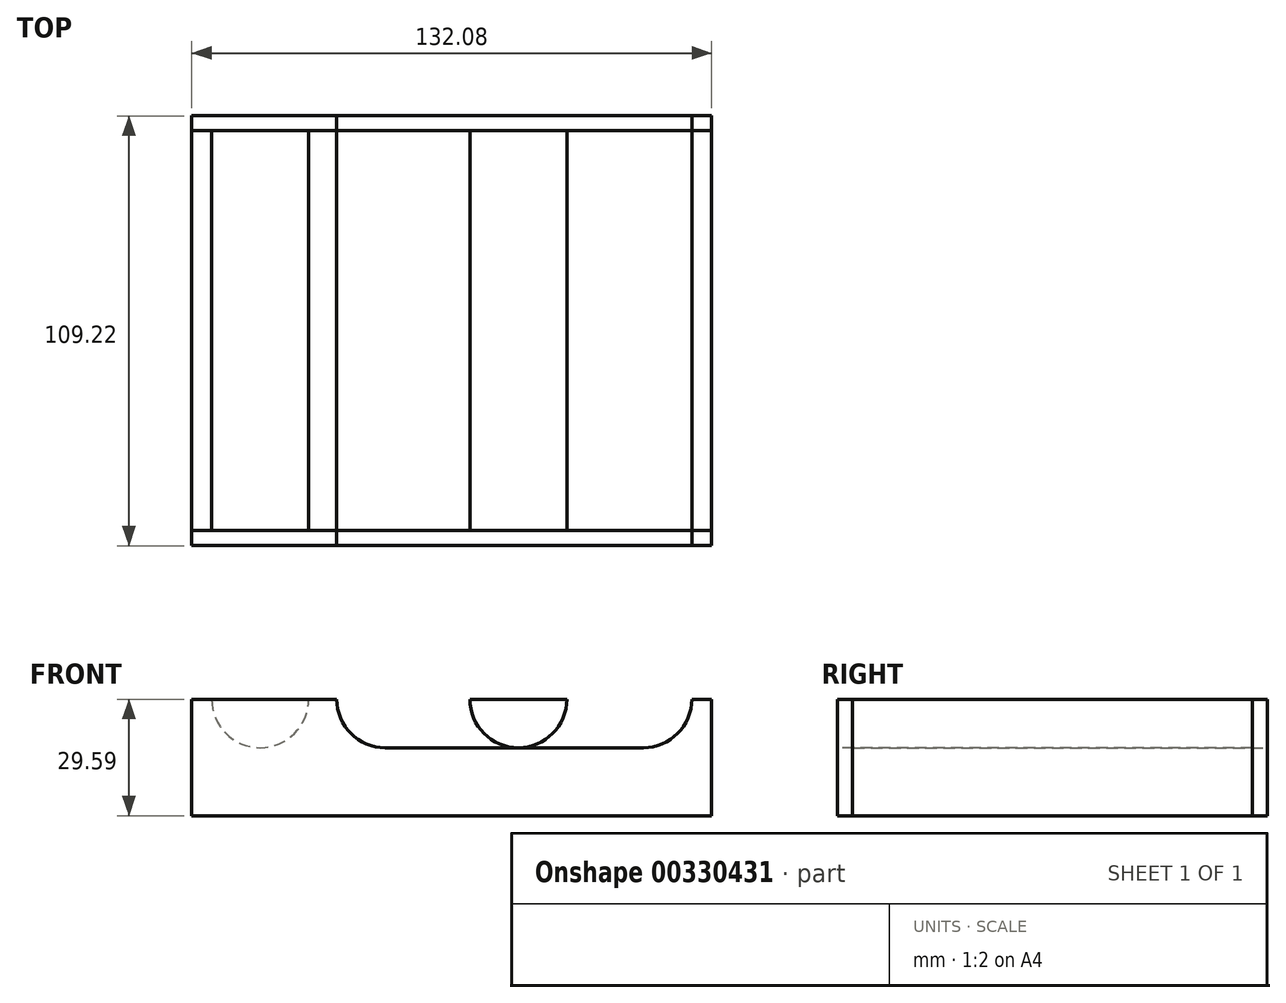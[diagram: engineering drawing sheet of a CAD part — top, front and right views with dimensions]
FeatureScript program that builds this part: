
annotation { "Feature Type Name" : "Feature", "Feature Type Description" : "" }
export const myFeature = defineFeature(function(context is Context, id is Id, definition is map)
    precondition{}
    {
        {
            var Q0;
            Q0=qCreatedBy(makeId("Top.planeOp"),FACE);
            var sketch = newSketch(context, id + "F0", { "sketchPlane" : qUnion([Q0])});
            skLineSegment(sketch, "E0.bottom", {"start": v(-43.55, 68.97) * mm, "end": v(88.53, 68.97) * mm});
            skLineSegment(sketch, "E0.top", {"start": v(-43.55, -32.63) * mm, "end": v(88.53, -32.63) * mm});
            skLineSegment(sketch, "E0.left", {"start": v(-43.55, 68.97) * mm, "end": v(-43.55, -32.63) * mm});
            skLineSegment(sketch, "E0.right", {"start": v(88.53, 68.97) * mm, "end": v(88.53, -32.63) * mm});
            skSolve(sketch);
        }
        {
            var Q0;
            Q0=makeQuery(id+"F0.imprint","IMPRINT",FACE,{"disambiguationData":[TD([[makeQuery(id+"F0.imprint","IMPRINT",EDGE,{"derivedFrom":sQuery(id+"F0.wireOp",EDGE,"E0.bottom")}),-1.0]])]});
            extrude(context, id + "F1", {"entities" : qUnion([Q0]), "depth" : 17.27 * mm});
        }
        {
            var Q0;
            Q0=makeQuery(id+"F1.opExtrude","SWEPT_FACE",FACE,{"disambiguationData":[OSD([sQuery(id+"F0.wireOp",EDGE,"E0.top")])]});
            var sketch = newSketch(context, id + "F2", { "sketchPlane" : qUnion([Q0])});
            skLineSegment(sketch, "E1", {"start": v(-26.19, 47.06) * mm, "end": v(-26.19, 17.27) * mm, "construction": true});
            skCircle(sketch, "E2", {"center": v(-26.19, 29.6) * mm, "radius": 12.32 * mm});
            skLineSegment(sketch, "E3", {"start": v(22.49, 17.27) * mm, "end": v(22.49, 64.89) * mm, "construction": true});
            skPoint(sketch, "E3.endSnap0", {"position": v(22.49, 17.27) * mm});
            skCircle(sketch, "E4.1.0.0", {"center": v(5.56, 29.6) * mm, "radius": 12.32 * mm});
            skLineSegment(sketch, "E4.direction1", {"start": v(-26.19, 29.6) * mm, "end": v(5.56, 29.6) * mm, "construction": true});
            skCircle(sketch, "E5.MirrorC", {"center": v(39.41, 29.6) * mm, "radius": 12.32 * mm});
            skCircle(sketch, "E6.MirrorC", {"center": v(71.16, 29.6) * mm, "radius": 12.32 * mm});
            skLineSegment(sketch, "E7", {"start": v(-43.55, 17.27) * mm, "end": v(-43.55, 29.6) * mm});
            skLineSegment(sketch, "E8", {"start": v(-43.55, 29.6) * mm, "end": v(88.53, 29.6) * mm});
            skLineSegment(sketch, "E9", {"start": v(88.53, 29.6) * mm, "end": v(88.53, 17.27) * mm});
            skLineSegment(sketch, "E10", {"start": v(88.53, 17.27) * mm, "end": v(-43.55, 17.27) * mm});
            skSolve(sketch);
        }
        {
            var Q0;
            {var subQ5=sQuery(id+"F2.wireOp",EDGE,"E9");Q0=makeQuery(id+"F2.imprint","IMPRINT",FACE,{"disambiguationData":[TD([[makeQuery(id+"F2.imprint","IMPRINT",EDGE,{"derivedFrom":subQ5}),-1.0]])]});}
            var Q1;
            {var subQ0=sQuery(id+"F2.wireOp",EDGE,"E8");var subQ1=sQuery(id+"F2.wireOp",EDGE,"E5.MirrorC");var subQ2=makeQuery(id+"F2.imprint","INTERSECT",VERTEX,{"disambiguationData":[OD(0.0)],"derivedFrom":[subQ1,subQ0]});Q1=makeQuery(id+"F2.imprint","IMPRINT",FACE,{"disambiguationData":[TD([[makeQuery(id+"F2.imprint","IMPRINT",EDGE,{"disambiguationData":[TD([[subQ2,-1.0]])],"derivedFrom":subQ1}),1.0]])]});}
            var Q2;
            {var subQ0=sQuery(id+"F2.wireOp",EDGE,"E8");var subQ1=sQuery(id+"F2.wireOp",EDGE,"E4.1.0.0");var subQ2=makeQuery(id+"F2.imprint","INTERSECT",VERTEX,{"disambiguationData":[OD(1.0)],"derivedFrom":[subQ1,subQ0]});Q2=makeQuery(id+"F2.imprint","IMPRINT",FACE,{"disambiguationData":[TD([[makeQuery(id+"F2.imprint","IMPRINT",EDGE,{"disambiguationData":[TD([[subQ2,1.0]])],"derivedFrom":subQ1}),-1.0]])]});}
            var Q3;
            {var subQ0=sQuery(id+"F2.wireOp",EDGE,"E8");var subQ1=sQuery(id+"F2.wireOp",EDGE,"E2");var subQ2=makeQuery(id+"F2.imprint","INTERSECT",VERTEX,{"disambiguationData":[OD(1.0)],"derivedFrom":[subQ1,subQ0]});Q3=makeQuery(id+"F2.imprint","IMPRINT",FACE,{"disambiguationData":[TD([[makeQuery(id+"F2.imprint","IMPRINT",EDGE,{"disambiguationData":[TD([[subQ2,1.0]])],"derivedFrom":subQ1}),-1.0]])]});}
            var Q4;
            {var subQ5=sQuery(id+"F2.wireOp",EDGE,"E7");Q4=makeQuery(id+"F2.imprint","IMPRINT",FACE,{"disambiguationData":[TD([[makeQuery(id+"F2.imprint","IMPRINT",EDGE,{"derivedFrom":subQ5}),-1.0]])]});}
            var Q5;
            Q5=makeQuery(id+"F1.opExtrude","SWEPT_FACE",FACE,{"disambiguationData":[OSD([sQuery(id+"F0.wireOp",EDGE,"E0.bottom")])]});
            extrude(context, id + "F3", {"entities" : qUnion([Q0, Q1, Q2, Q3, Q4]), "operationType" : NewBodyOperationType.ADD, "endBound" : BoundingType.UP_TO_SURFACE, "oppositeDirection" : true, "endBoundEntityFace" : qUnion([Q5]), "depth" : 53.34 * mm});
        }
        {
            var Q0;
            {var subQ0=sQuery(id+"F2.wireOp",EDGE,"E10");var subQ1=sQuery(id+"F2.wireOp",EDGE,"E8");var subQ2=sQuery(id+"F2.wireOp",EDGE,"E6.MirrorC");var subQ3=sQuery(id+"F2.wireOp",EDGE,"E5.MirrorC");var subQ4=sQuery(id+"F2.wireOp",EDGE,"E4.1.0.0");var subQ5=sQuery(id+"F2.wireOp",EDGE,"E2");Q0=makeQuery(id+"F3.boolean.opBoolean","MERGE",FACE,{"derivedFrom":[makeQuery(id+"F1.opExtrude","SWEPT_FACE",FACE,{"disambiguationData":[OSD([sQuery(id+"F0.wireOp",EDGE,"E0.top")])]}),makeQuery(id+"F3.opExtrude","CAP_FACE",FACE,{"disambiguationData":[OSD([subQ5,sQuery(id+"F2.wireOp",EDGE,"E7"),subQ1,subQ0])],"isStart":true}),makeQuery(id+"F3.opExtrude","CAP_FACE",FACE,{"disambiguationData":[OSD([subQ5,subQ4,subQ1,subQ0])],"isStart":true}),makeQuery(id+"F3.opExtrude","CAP_FACE",FACE,{"disambiguationData":[OSD([subQ4,subQ3,subQ1,subQ0])],"isStart":true}),makeQuery(id+"F3.opExtrude","CAP_FACE",FACE,{"disambiguationData":[OSD([subQ3,subQ2,subQ1,subQ0])],"isStart":true}),makeQuery(id+"F3.opExtrude","CAP_FACE",FACE,{"disambiguationData":[OSD([subQ2,subQ1,sQuery(id+"F2.wireOp",EDGE,"E9"),subQ0])],"isStart":true})]});}
            var Q1;
            {var subQ0=sQuery(id+"F2.wireOp",EDGE,"E10");var subQ1=sQuery(id+"F2.wireOp",EDGE,"E8");var subQ2=sQuery(id+"F2.wireOp",EDGE,"E6.MirrorC");var subQ3=sQuery(id+"F0.wireOp",EDGE,"E0.bottom");var subQ4=sQuery(id+"F2.wireOp",EDGE,"E5.MirrorC");var subQ5=sQuery(id+"F2.wireOp",EDGE,"E4.1.0.0");var subQ6=sQuery(id+"F2.wireOp",EDGE,"E2");Q1=makeQuery(id+"F3.boolean.opBoolean","MERGE",FACE,{"derivedFrom":[makeQuery(id+"F1.opExtrude","SWEPT_FACE",FACE,{"disambiguationData":[OSD([subQ3])]}),makeQuery(id+"F3.opExtrude","CAP_FACE",FACE,{"disambiguationData":[OSD([subQ3]),ownerDisambiguation([makeQuery(id+"F3.opExtrude","SWEPT_BODY",BODY,{"disambiguationData":[OSD([subQ6,sQuery(id+"F2.wireOp",EDGE,"E7"),subQ1,subQ0])]})])],"isStart":false}),makeQuery(id+"F3.opExtrude","CAP_FACE",FACE,{"disambiguationData":[OSD([subQ3]),ownerDisambiguation([makeQuery(id+"F3.opExtrude","SWEPT_BODY",BODY,{"disambiguationData":[OSD([subQ6,subQ5,subQ1,subQ0])]})])],"isStart":false}),makeQuery(id+"F3.opExtrude","CAP_FACE",FACE,{"disambiguationData":[OSD([subQ3]),ownerDisambiguation([makeQuery(id+"F3.opExtrude","SWEPT_BODY",BODY,{"disambiguationData":[OSD([subQ5,subQ4,subQ1,subQ0])]})])],"isStart":false}),makeQuery(id+"F3.opExtrude","CAP_FACE",FACE,{"disambiguationData":[OSD([subQ3]),ownerDisambiguation([makeQuery(id+"F3.opExtrude","SWEPT_BODY",BODY,{"disambiguationData":[OSD([subQ4,subQ2,subQ1,subQ0])]})])],"isStart":false}),makeQuery(id+"F3.opExtrude","CAP_FACE",FACE,{"disambiguationData":[OSD([subQ3]),ownerDisambiguation([makeQuery(id+"F3.opExtrude","SWEPT_BODY",BODY,{"disambiguationData":[OSD([subQ2,subQ1,sQuery(id+"F2.wireOp",EDGE,"E9"),subQ0])]})])],"isStart":false})]});}
            cPlane(context, id + "F4", {"entities" : qUnion([Q0, Q1]), "cplaneType" : CPlaneType.MID_PLANE, "offset" : 25.4 * mm, "width" : 152.4 * mm, "height" : 152.4 * mm});
        }
        {
            var Q0;
            {var subQ0=sQuery(id+"F2.wireOp",EDGE,"E10");var subQ1=sQuery(id+"F2.wireOp",EDGE,"E8");var subQ2=sQuery(id+"F2.wireOp",EDGE,"E6.MirrorC");var subQ3=sQuery(id+"F2.wireOp",EDGE,"E5.MirrorC");var subQ4=sQuery(id+"F2.wireOp",EDGE,"E4.1.0.0");var subQ5=sQuery(id+"F2.wireOp",EDGE,"E2");Q0=makeQuery(id+"F3.boolean.opBoolean","MERGE",FACE,{"derivedFrom":[makeQuery(id+"F1.opExtrude","SWEPT_FACE",FACE,{"disambiguationData":[OSD([sQuery(id+"F0.wireOp",EDGE,"E0.top")])]}),makeQuery(id+"F3.opExtrude","CAP_FACE",FACE,{"disambiguationData":[OSD([subQ5,sQuery(id+"F2.wireOp",EDGE,"E7"),subQ1,subQ0])],"isStart":true}),makeQuery(id+"F3.opExtrude","CAP_FACE",FACE,{"disambiguationData":[OSD([subQ5,subQ4,subQ1,subQ0])],"isStart":true}),makeQuery(id+"F3.opExtrude","CAP_FACE",FACE,{"disambiguationData":[OSD([subQ4,subQ3,subQ1,subQ0])],"isStart":true}),makeQuery(id+"F3.opExtrude","CAP_FACE",FACE,{"disambiguationData":[OSD([subQ3,subQ2,subQ1,subQ0])],"isStart":true}),makeQuery(id+"F3.opExtrude","CAP_FACE",FACE,{"disambiguationData":[OSD([subQ2,subQ1,sQuery(id+"F2.wireOp",EDGE,"E9"),subQ0])],"isStart":true})]});}
            var sketch = newSketch(context, id + "F5", { "sketchPlane" : qUnion([Q0])});
            skLineSegment(sketch, "E11.bottom", {"start": v(88.53, 0) * mm, "end": v(-43.55, 0) * mm});
            skLineSegment(sketch, "E11.top", {"start": v(88.53, 29.6) * mm, "end": v(-43.55, 29.6) * mm});
            skLineSegment(sketch, "E11.left", {"start": v(88.53, 0) * mm, "end": v(88.53, 29.6) * mm});
            skLineSegment(sketch, "E11.right", {"start": v(-43.55, 0) * mm, "end": v(-43.55, 29.6) * mm});
            skSolve(sketch);
        }
        {
            var Q0;
            {var subQ1=sQuery(id+"F2.wireOp",EDGE,"E8");var subQ2=sQuery(id+"F2.wireOp",EDGE,"E2");var subQ4=makeQuery(id+"F3.boolean.opBoolean","MERGE",EDGE,{"derivedFrom":[makeQuery(id+"F3.opExtrude","CAP_EDGE",EDGE,{"disambiguationData":[OSD([subQ2]),TDD([makeQuery(id+"F2.imprint","IMPRINT",EDGE,{"disambiguationData":[TD([[makeQuery(id+"F2.imprint","INTERSECT",VERTEX,{"disambiguationData":[OD(0.0)],"derivedFrom":[subQ2,subQ1]}),-1.0]])],"derivedFrom":subQ2})])],"isStart":true}),makeQuery(id+"F3.opExtrude","CAP_EDGE",EDGE,{"disambiguationData":[OSD([subQ2]),TDD([makeQuery(id+"F2.imprint","IMPRINT",EDGE,{"disambiguationData":[TD([[makeQuery(id+"F2.imprint","INTERSECT",VERTEX,{"disambiguationData":[OD(1.0)],"derivedFrom":[subQ2,subQ1]}),1.0]])],"derivedFrom":subQ2})])],"isStart":true})]});Q0=makeQuery(id+"F5.imprint","IMPRINT",FACE,{"disambiguationData":[TD([[makeQuery(id+"F5.imprint","IMPRINT",EDGE,{"derivedFrom":subQ4}),1.0]])]});}
            var Q1;
            {var subQ1=sQuery(id+"F2.wireOp",EDGE,"E8");var subQ2=sQuery(id+"F2.wireOp",EDGE,"E4.1.0.0");var subQ4=makeQuery(id+"F3.boolean.opBoolean","MERGE",EDGE,{"derivedFrom":[makeQuery(id+"F3.opExtrude","CAP_EDGE",EDGE,{"disambiguationData":[OSD([subQ2]),TDD([makeQuery(id+"F2.imprint","IMPRINT",EDGE,{"disambiguationData":[TD([[makeQuery(id+"F2.imprint","INTERSECT",VERTEX,{"disambiguationData":[OD(0.0)],"derivedFrom":[subQ2,subQ1]}),-1.0]])],"derivedFrom":subQ2})])],"isStart":true}),makeQuery(id+"F3.opExtrude","CAP_EDGE",EDGE,{"disambiguationData":[OSD([subQ2]),TDD([makeQuery(id+"F2.imprint","IMPRINT",EDGE,{"disambiguationData":[TD([[makeQuery(id+"F2.imprint","INTERSECT",VERTEX,{"disambiguationData":[OD(1.0)],"derivedFrom":[subQ2,subQ1]}),1.0]])],"derivedFrom":subQ2})])],"isStart":true})]});Q1=makeQuery(id+"F5.imprint","IMPRINT",FACE,{"disambiguationData":[TD([[makeQuery(id+"F5.imprint","IMPRINT",EDGE,{"derivedFrom":subQ4}),1.0]])]});}
            var Q2;
            {var subQ1=sQuery(id+"F2.wireOp",EDGE,"E8");var subQ2=sQuery(id+"F2.wireOp",EDGE,"E5.MirrorC");var subQ4=makeQuery(id+"F3.boolean.opBoolean","MERGE",EDGE,{"derivedFrom":[makeQuery(id+"F3.opExtrude","CAP_EDGE",EDGE,{"disambiguationData":[OSD([subQ2]),TDD([makeQuery(id+"F2.imprint","IMPRINT",EDGE,{"disambiguationData":[TD([[makeQuery(id+"F2.imprint","INTERSECT",VERTEX,{"disambiguationData":[OD(0.0)],"derivedFrom":[subQ2,subQ1]}),-1.0]])],"derivedFrom":subQ2})])],"isStart":true}),makeQuery(id+"F3.opExtrude","CAP_EDGE",EDGE,{"disambiguationData":[OSD([subQ2]),TDD([makeQuery(id+"F2.imprint","IMPRINT",EDGE,{"disambiguationData":[TD([[makeQuery(id+"F2.imprint","INTERSECT",VERTEX,{"disambiguationData":[OD(1.0)],"derivedFrom":[subQ2,subQ1]}),1.0]])],"derivedFrom":subQ2})])],"isStart":true})]});Q2=makeQuery(id+"F5.imprint","IMPRINT",FACE,{"disambiguationData":[TD([[makeQuery(id+"F5.imprint","IMPRINT",EDGE,{"derivedFrom":subQ4}),-1.0]])]});}
            var Q3;
            {var subQ1=sQuery(id+"F2.wireOp",EDGE,"E8");var subQ2=sQuery(id+"F2.wireOp",EDGE,"E6.MirrorC");var subQ4=makeQuery(id+"F3.boolean.opBoolean","MERGE",EDGE,{"derivedFrom":[makeQuery(id+"F3.opExtrude","CAP_EDGE",EDGE,{"disambiguationData":[OSD([subQ2]),TDD([makeQuery(id+"F2.imprint","IMPRINT",EDGE,{"disambiguationData":[TD([[makeQuery(id+"F2.imprint","INTERSECT",VERTEX,{"disambiguationData":[OD(0.0)],"derivedFrom":[subQ2,subQ1]}),-1.0]])],"derivedFrom":subQ2})])],"isStart":true}),makeQuery(id+"F3.opExtrude","CAP_EDGE",EDGE,{"disambiguationData":[OSD([subQ2]),TDD([makeQuery(id+"F2.imprint","IMPRINT",EDGE,{"disambiguationData":[TD([[makeQuery(id+"F2.imprint","INTERSECT",VERTEX,{"disambiguationData":[OD(1.0)],"derivedFrom":[subQ2,subQ1]}),1.0]])],"derivedFrom":subQ2})])],"isStart":true})]});Q3=makeQuery(id+"F5.imprint","IMPRINT",FACE,{"disambiguationData":[TD([[makeQuery(id+"F5.imprint","IMPRINT",EDGE,{"derivedFrom":subQ4}),-1.0]])]});}
            var Q4;
            Q4=makeQuery(id+"F5.imprint","IMPRINT",FACE,{"disambiguationData":[TD([[makeQuery(id+"F5.imprint","IMPRINT",EDGE,{"derivedFrom":sQuery(id+"F5.wireOp",EDGE,"E11.bottom")}),1.0]])]});
            extrude(context, id + "F6", {"entities" : qUnion([Q0, Q1, Q2, Q3, Q4]), "operationType" : NewBodyOperationType.ADD, "depth" : 3.8 * mm});
        }
        {
            var Q0;
            Q0=makeQuery(id+"F1.opExtrude","SWEPT_BODY",BODY,{"disambiguationData":[OSD([sQuery(id+"F0.wireOp",EDGE,"E0.bottom"),sQuery(id+"F0.wireOp",EDGE,"E0.top"),sQuery(id+"F0.wireOp",EDGE,"E0.left"),sQuery(id+"F0.wireOp",EDGE,"E0.right")])]});
            var Q1;
            Q1=qCreatedBy(id+"F4.planeOp",FACE);
            mirror(context, id + "F7", {"operationType" : NewBodyOperationType.ADD, "entities" : qUnion([Q0]), "mirrorPlane" : qUnion([Q1])});
        }
    });
